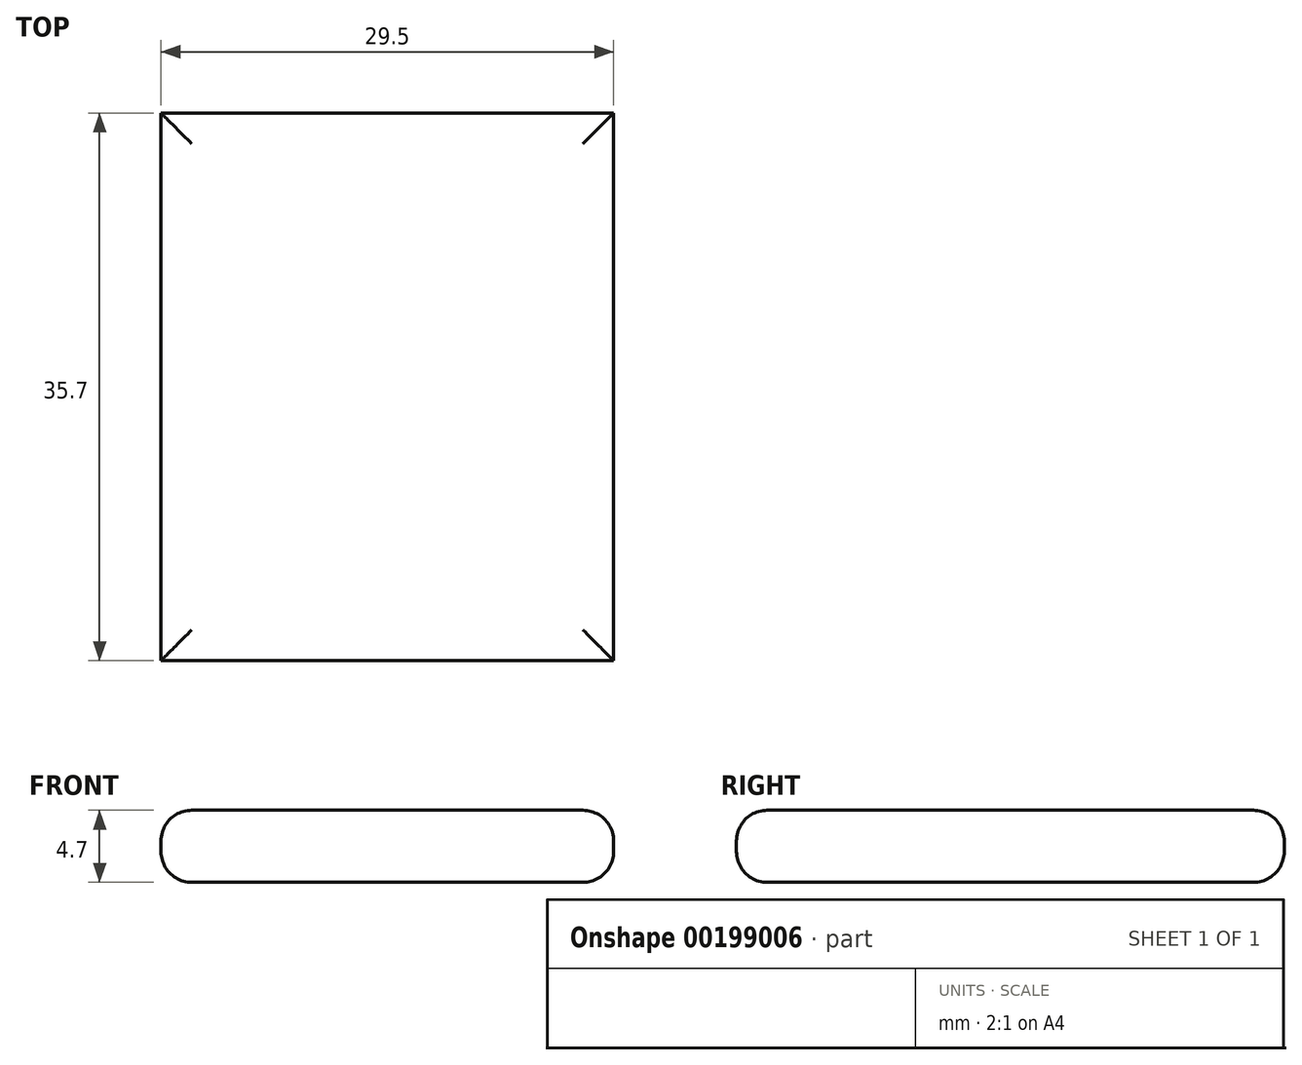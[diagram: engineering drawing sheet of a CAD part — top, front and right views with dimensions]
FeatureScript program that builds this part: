
annotation { "Feature Type Name" : "Feature", "Feature Type Description" : "" }
export const myFeature = defineFeature(function(context is Context, id is Id, definition is map)
    precondition{}
    {
        {
            var Q0;
            Q0=qCreatedBy(makeId("Top.planeOp"),FACE);
            var sketch = newSketch(context, id + "F0", { "sketchPlane" : qUnion([Q0])});
            skLineSegment(sketch, "E0.bottom", {"start": v(14.75, 17.85) * mm, "end": v(-14.75, 17.85) * mm});
            skLineSegment(sketch, "E0.top", {"start": v(14.75, -17.85) * mm, "end": v(-14.75, -17.85) * mm});
            skLineSegment(sketch, "E0.left", {"start": v(14.75, 17.85) * mm, "end": v(14.75, -17.85) * mm});
            skLineSegment(sketch, "E0.right", {"start": v(-14.75, 17.85) * mm, "end": v(-14.75, -17.85) * mm});
            skPoint(sketch, "E0.middle", {"position": v(0, 0) * mm});
            skSolve(sketch);
        }
        {
            var Q0;
            Q0=makeQuery(id+"F0.imprint","IMPRINT",FACE,{"disambiguationData":[TD([[makeQuery(id+"F0.imprint","IMPRINT",EDGE,{"derivedFrom":sQuery(id+"F0.wireOp",EDGE,"E0.bottom")}),1.0]])]});
            extrude(context, id + "F1", {"entities" : qUnion([Q0]), "depth" : 4.7 * mm, "symmetric" : true});
        }
        {
            var Q0;
            Q0=makeQuery(id+"F1.opExtrude","CAP_EDGE",EDGE,{"disambiguationData":[OSD([sQuery(id+"F0.wireOp",EDGE,"E0.top")])],"isStart":false});
            var Q1;
            Q1=makeQuery(id+"F1.opExtrude","CAP_EDGE",EDGE,{"disambiguationData":[OSD([sQuery(id+"F0.wireOp",EDGE,"E0.right")])],"isStart":false});
            var Q2;
            Q2=makeQuery(id+"F1.opExtrude","CAP_EDGE",EDGE,{"disambiguationData":[OSD([sQuery(id+"F0.wireOp",EDGE,"E0.bottom")])],"isStart":false});
            var Q3;
            Q3=makeQuery(id+"F1.opExtrude","CAP_EDGE",EDGE,{"disambiguationData":[OSD([sQuery(id+"F0.wireOp",EDGE,"E0.left")])],"isStart":false});
            var Q4;
            Q4=makeQuery(id+"F1.opExtrude","CAP_EDGE",EDGE,{"disambiguationData":[OSD([sQuery(id+"F0.wireOp",EDGE,"E0.left")])],"isStart":true});
            var Q5;
            Q5=makeQuery(id+"F1.opExtrude","CAP_EDGE",EDGE,{"disambiguationData":[OSD([sQuery(id+"F0.wireOp",EDGE,"E0.top")])],"isStart":true});
            var Q6;
            Q6=makeQuery(id+"F1.opExtrude","CAP_EDGE",EDGE,{"disambiguationData":[OSD([sQuery(id+"F0.wireOp",EDGE,"E0.bottom")])],"isStart":true});
            var Q7;
            Q7=makeQuery(id+"F1.opExtrude","CAP_EDGE",EDGE,{"disambiguationData":[OSD([sQuery(id+"F0.wireOp",EDGE,"E0.right")])],"isStart":true});
            fillet(context, id + "F2", {"entities" : qUnion([Q0, Q1, Q2, Q3, Q4, Q5, Q6, Q7]), "radius" : 2 * mm, "tangentPropagation" : true, "allowEdgeOverflow" : false});
        }
    });
